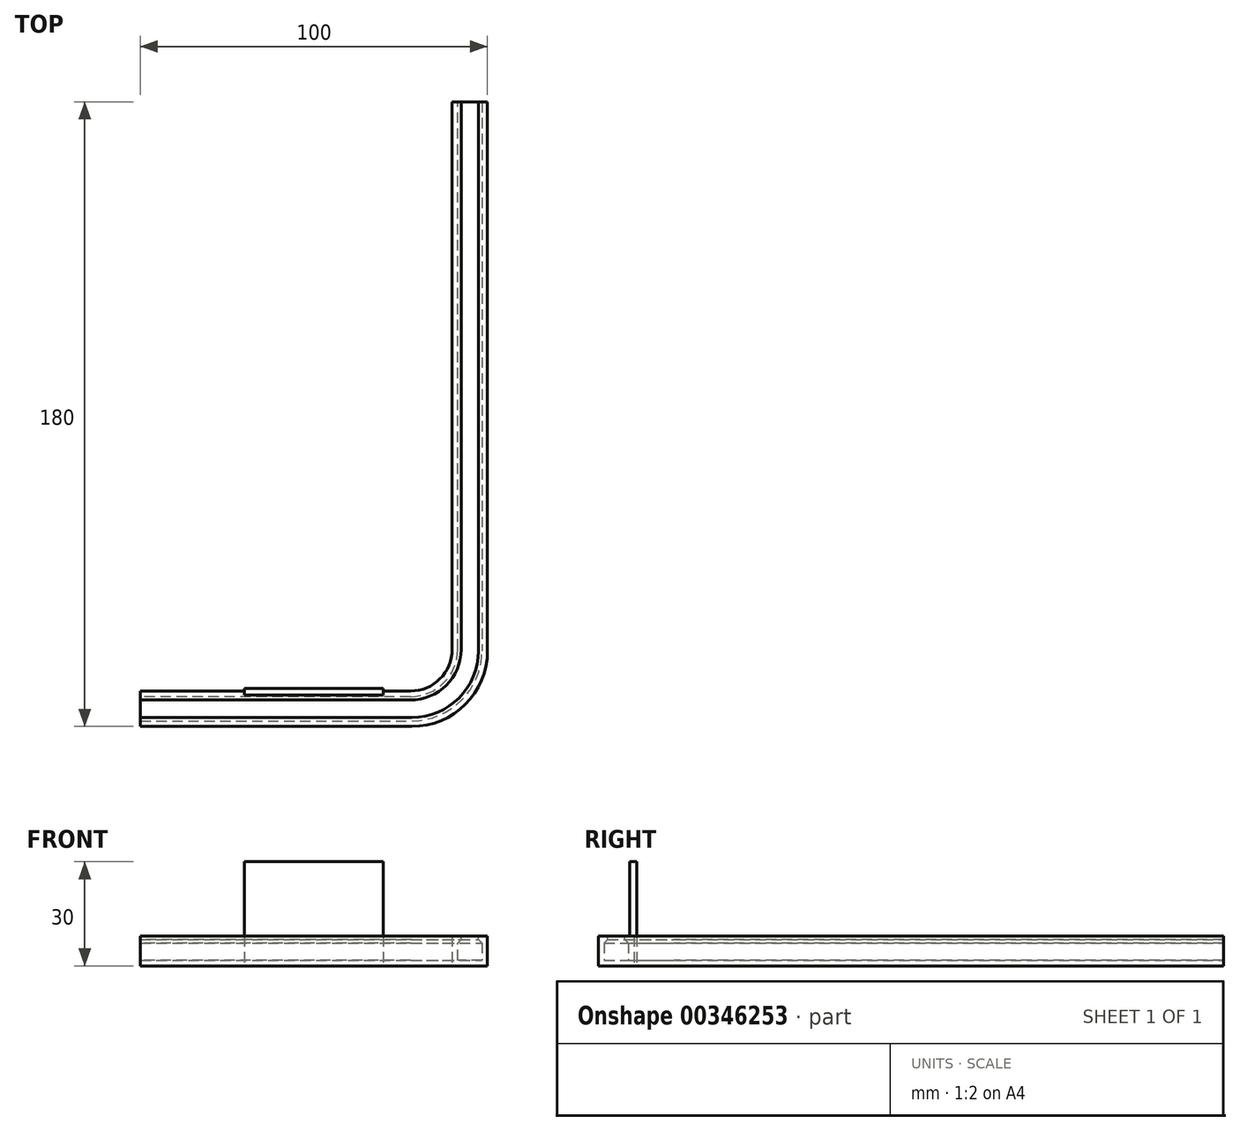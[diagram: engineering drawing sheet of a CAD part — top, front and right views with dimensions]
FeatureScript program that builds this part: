
annotation { "Feature Type Name" : "Feature", "Feature Type Description" : "" }
export const myFeature = defineFeature(function(context is Context, id is Id, definition is map)
    precondition{}
    {
        {
            var Q0;
            Q0=qCreatedBy(makeId("Top.planeOp"),FACE);
            var sketch = newSketch(context, id + "F0", { "sketchPlane" : qUnion([Q0])});
            skLineSegment(sketch, "E0", {"start": v(0, 180) * mm, "end": v(0, 0) * mm});
            skLineSegment(sketch, "E1", {"start": v(-100, 0) * mm, "end": v(0, 0) * mm});
            skLineSegment(sketch, "E2", {"start": v(-100, 0) * mm, "end": v(-100, 10.2) * mm});
            skLineSegment(sketch, "E3", {"start": v(-10.2, 10.2) * mm, "end": v(-100, 10.2) * mm});
            skLineSegment(sketch, "E4", {"start": v(-10.2, 10.2) * mm, "end": v(-10.2, 180) * mm});
            skLineSegment(sketch, "E5", {"start": v(0, 180) * mm, "end": v(-10.2, 180) * mm});
            skSolve(sketch);
        }
        {
            var Q0;
            Q0 = qSketchRegion(id + "F0", true);
            extrude(context, id + "F1", {"entities" : qUnion([Q0]), "depth" : 8.6 * mm});
        }
        {
            var Q0;
            Q0=makeQuery(id+"F1.opExtrude","SWEPT_EDGE",EDGE,{"disambiguationData":[OSD([sQuery(id+"F0.wireOp",EDGE,"E3"),sQuery(id+"F0.wireOp",EDGE,"E4")])]});
            fillet(context, id + "F2", {"entities" : qUnion([Q0]), "radius" : 12 * mm, "tangentPropagation" : true, "allowEdgeOverflow" : false});
        }
        {
            var Q0;
            Q0=makeQuery(id+"F1.opExtrude","SWEPT_EDGE",EDGE,{"disambiguationData":[OSD([sQuery(id+"F0.wireOp",EDGE,"E0"),sQuery(id+"F0.wireOp",EDGE,"E1")])]});
            fillet(context, id + "F3", {"entities" : qUnion([Q0]), "radius" : 21.8 * mm, "tangentPropagation" : true, "allowEdgeOverflow" : false});
        }
        {
            var Q0;
            Q0=makeQuery(id+"F1.opExtrude","SWEPT_FACE",FACE,{"disambiguationData":[OSD([sQuery(id+"F0.wireOp",EDGE,"E2")])]});
            var Q1;
            Q1=makeQuery(id+"F1.opExtrude","CAP_FACE",FACE,{"disambiguationData":[OSD([sQuery(id+"F0.wireOp",EDGE,"E0"),sQuery(id+"F0.wireOp",EDGE,"E1"),sQuery(id+"F0.wireOp",EDGE,"E2"),sQuery(id+"F0.wireOp",EDGE,"E3"),sQuery(id+"F0.wireOp",EDGE,"E4"),sQuery(id+"F0.wireOp",EDGE,"E5")])],"isStart":false});
            var Q2;
            Q2=makeQuery(id+"F1.opExtrude","SWEPT_FACE",FACE,{"disambiguationData":[OSD([sQuery(id+"F0.wireOp",EDGE,"E5")])]});
            shell(context, id + "F4", {"entities" : qUnion([Q0, Q1, Q2]), "thickness" : 1.6 * mm});
        }
        {
            var Q0;
            {var subQ0=sQuery(id+"F0.wireOp",EDGE,"E5");var subQ1=sQuery(id+"F0.wireOp",EDGE,"E4");var subQ2=sQuery(id+"F0.wireOp",EDGE,"E3");var subQ3=sQuery(id+"F0.wireOp",EDGE,"E2");var subQ4=sQuery(id+"F0.wireOp",EDGE,"E1");var subQ5=sQuery(id+"F0.wireOp",EDGE,"E0");Q0=makeQuery(id+"F4.opShell","OFFSET_FACE",FACE,{"disambiguationData":[OSD([subQ5,subQ4,subQ3,subQ2,subQ1,subQ0]),TDD([makeQuery(id+"F1.opExtrude","CAP_FACE",FACE,{"disambiguationData":[OSD([subQ5,subQ4,subQ3,subQ2,subQ1,subQ0])],"isStart":false})])]});}
            var sketch = newSketch(context, id + "F5", { "sketchPlane" : qUnion([Q0])});
            skLineSegment(sketch, "E6.0", {"start": v(-7.6, 22.2) * mm, "end": v(-7.6, 180) * mm});
            skArc(sketch, "E6.1", {"start": v(-7.6, 22.2) * mm, "mid": v(-11.88, 11.88) * mm, "end": v(-22.2, 7.6) * mm});
            skLineSegment(sketch, "E6.2", {"start": v(-22.2, 7.6) * mm, "end": v(-100, 7.6) * mm});
            skLineSegment(sketch, "E7.0", {"start": v(-10.2, 22.2) * mm, "end": v(-10.2, 180) * mm});
            skArc(sketch, "E8.0", {"start": v(-10.2, 22.2) * mm, "mid": v(-13.71, 13.71) * mm, "end": v(-22.2, 10.2) * mm});
            skLineSegment(sketch, "E9.0", {"start": v(-22.2, 10.2) * mm, "end": v(-100, 10.2) * mm});
            skLineSegment(sketch, "E10", {"start": v(-100, 7.6) * mm, "end": v(-100, 10.2) * mm});
            skLineSegment(sketch, "E11", {"start": v(-7.6, 180) * mm, "end": v(-10.2, 180) * mm});
            skLineSegment(sketch, "E12.0", {"start": v(0, 180) * mm, "end": v(0, 21.8) * mm});
            skArc(sketch, "E13.0", {"start": v(-21.8, 0) * mm, "mid": v(-6.39, 6.39) * mm, "end": v(0, 21.8) * mm});
            skLineSegment(sketch, "E14.0.2", {"start": v(-100, 0) * mm, "end": v(-21.8, 0) * mm});
            skLineSegment(sketch, "E14.0.4", {"start": v(0, 21.8) * mm, "end": v(0, 180) * mm});
            skLineSegment(sketch, "E15.0", {"start": v(-100, 2.6) * mm, "end": v(-21.8, 2.6) * mm});
            skArc(sketch, "E15.1", {"start": v(-21.8, 2.6) * mm, "mid": v(-8.22, 8.22) * mm, "end": v(-2.6, 21.8) * mm});
            skLineSegment(sketch, "E15.2", {"start": v(-2.6, 180) * mm, "end": v(-2.6, 21.8) * mm});
            skLineSegment(sketch, "E16", {"start": v(-100, 0) * mm, "end": v(-100, 2.6) * mm});
            skLineSegment(sketch, "E17", {"start": v(-2.6, 180) * mm, "end": v(0, 180) * mm});
            skSolve(sketch);
        }
        {
            var Q0;
            Q0 = qSketchRegion(id + "F5", true);
            extrude(context, id + "F6", {"entities" : qUnion([Q0]), "operationType" : NewBodyOperationType.ADD, "oppositeDirection" : true, "depth" : 2 * mm});
        }
        {
            var Q0;
            Q0=makeQuery(id+"F6.opExtrude","CAP_EDGE",EDGE,{"disambiguationData":[OSD([sQuery(id+"F5.wireOp",EDGE,"E6.2")])],"isStart":false});
            var Q1;
            Q1=makeQuery(id+"F6.opExtrude","CAP_EDGE",EDGE,{"disambiguationData":[OSD([sQuery(id+"F5.wireOp",EDGE,"E15.0")])],"isStart":false});
            chamfer(context, id + "F7", {"entities" : qUnion([Q0, Q1]), "width" : 1 * mm, "tangentPropagation" : true});
        }
        {
            var Q0;
            Q0=qCreatedBy(makeId("Top.planeOp"),FACE);
            var sketch = newSketch(context, id + "F8", { "sketchPlane" : qUnion([Q0])});
            skLineSegment(sketch, "E18.bottom", {"start": v(-30, 9) * mm, "end": v(-70, 9) * mm});
            skLineSegment(sketch, "E18.top", {"start": v(-30, 11) * mm, "end": v(-70, 11) * mm});
            skLineSegment(sketch, "E18.left", {"start": v(-30, 9) * mm, "end": v(-30, 11) * mm});
            skLineSegment(sketch, "E18.right", {"start": v(-70, 9) * mm, "end": v(-70, 11) * mm});
            skSolve(sketch);
        }
        {
            var Q0;
            Q0 = qSketchRegion(id + "F8", true);
            extrude(context, id + "F9", {"entities" : qUnion([Q0]), "operationType" : NewBodyOperationType.ADD, "depth" : 30 * mm});
        }
    });
